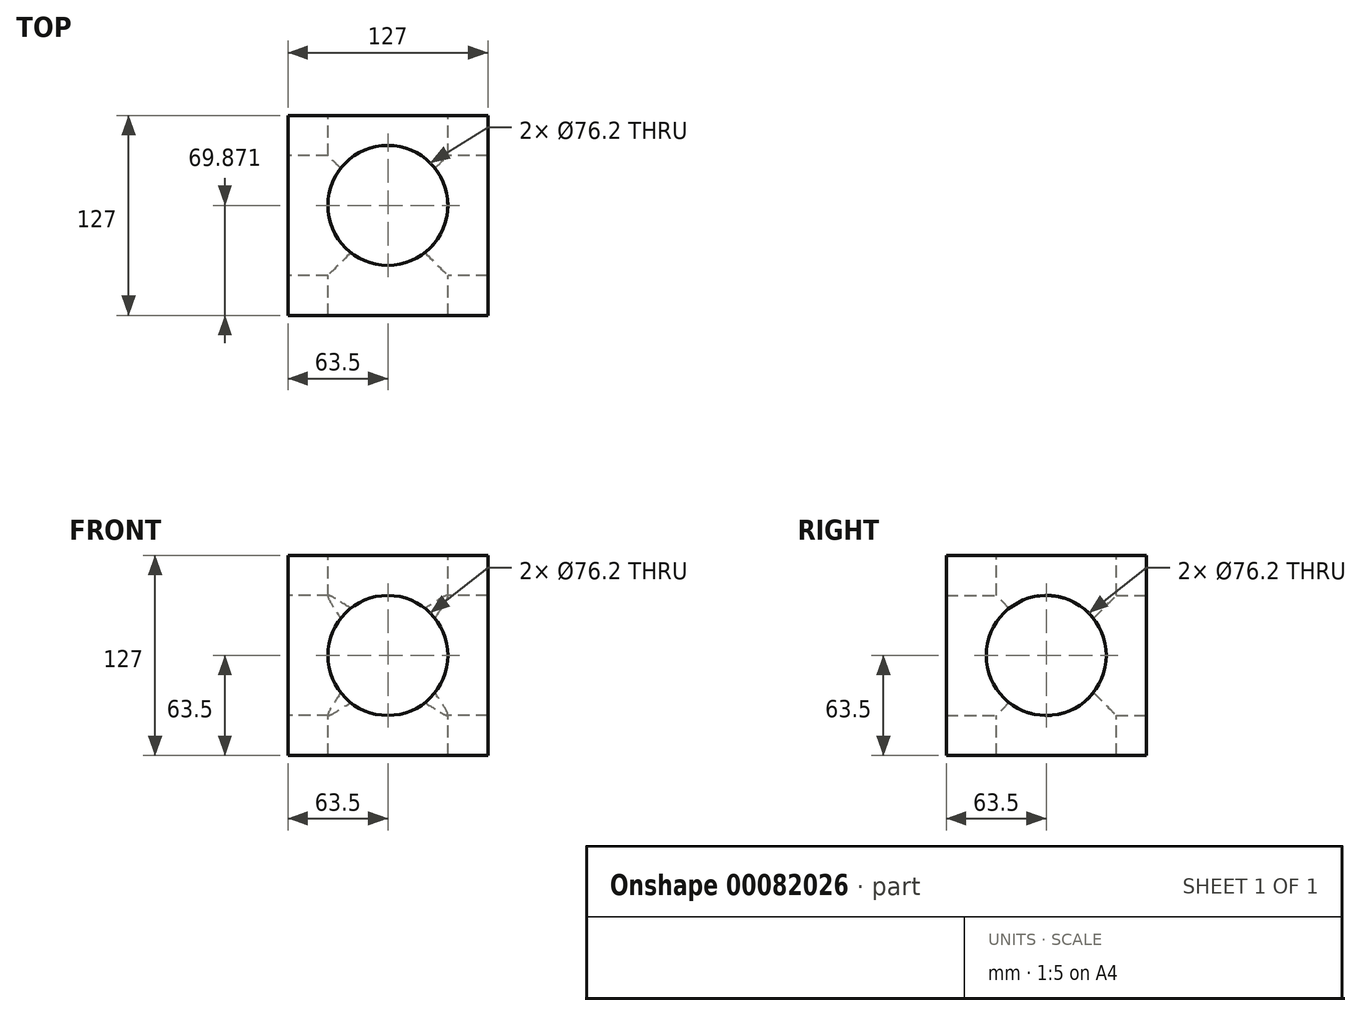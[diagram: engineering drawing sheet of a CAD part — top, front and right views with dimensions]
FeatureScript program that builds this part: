
annotation { "Feature Type Name" : "Feature", "Feature Type Description" : "" }
export const myFeature = defineFeature(function(context is Context, id is Id, definition is map)
    precondition{}
    {
        {
            var Q0;
            Q0=qCreatedBy(makeId("Top.planeOp"),FACE);
            var sketch = newSketch(context, id + "F0", { "sketchPlane" : qUnion([Q0])});
            skLineSegment(sketch, "E0", {"start": v(0, 0) * mm, "end": v(-127, 0) * mm});
            skLineSegment(sketch, "E1", {"start": v(-127, 0) * mm, "end": v(-127, 127) * mm});
            skLineSegment(sketch, "E2", {"start": v(-127, 127) * mm, "end": v(0, 127) * mm});
            skLineSegment(sketch, "E3", {"start": v(0, 0) * mm, "end": v(0, 127) * mm});
            skSolve(sketch);
        }
        {
            var Q0;
            Q0=makeQuery(id+"F0.imprint","IMPRINT",FACE,{"disambiguationData":[TD([[makeQuery(id+"F0.imprint","IMPRINT",EDGE,{"derivedFrom":sQuery(id+"F0.wireOp",EDGE,"E0")}),-1.0]])]});
            extrude(context, id + "F1", {"entities" : qUnion([Q0]), "depth" : 127 * mm});
        }
        {
            var Q0;
            Q0=makeQuery(id+"F1.opExtrude","SWEPT_FACE",FACE,{"disambiguationData":[OSD([sQuery(id+"F0.wireOp",EDGE,"E1")])]});
            var sketch = newSketch(context, id + "F2", { "sketchPlane" : qUnion([Q0])});
            skCircle(sketch, "E4", {"center": v(-63.5, 63.5) * mm, "radius": 38.1 * mm});
            skSolve(sketch);
        }
        {
            var Q0;
            Q0=makeQuery(id+"F1.opExtrude","SWEPT_FACE",FACE,{"disambiguationData":[OSD([sQuery(id+"F0.wireOp",EDGE,"E2")])]});
            var sketch = newSketch(context, id + "F3", { "sketchPlane" : qUnion([Q0])});
            skCircle(sketch, "E5", {"center": v(63.5, 63.5) * mm, "radius": 38.1 * mm});
            skSolve(sketch);
        }
        {
            var Q0;
            Q0=makeQuery(id+"F1.opExtrude","CAP_FACE",FACE,{"disambiguationData":[OSD([sQuery(id+"F0.wireOp",EDGE,"E0"),sQuery(id+"F0.wireOp",EDGE,"E1"),sQuery(id+"F0.wireOp",EDGE,"E2"),sQuery(id+"F0.wireOp",EDGE,"E3")])],"isStart":false});
            var sketch = newSketch(context, id + "F4", { "sketchPlane" : qUnion([Q0])});
            skCircle(sketch, "E6", {"center": v(-63.5, 69.87) * mm, "radius": 38.1 * mm});
            skPoint(sketch, "E7.orphan", {"position": v(-63.5, 127) * mm});
            skPoint(sketch, "E8.end.orphan", {"position": v(-63.5, 0) * mm});
            skSolve(sketch);
        }
        {
            var Q0;
            Q0=makeQuery(id+"F4.imprint","IMPRINT",FACE,{"disambiguationData":[TD([[makeQuery(id+"F4.imprint","IMPRINT",EDGE,{"derivedFrom":sQuery(id+"F4.wireOp",EDGE,"E6")}),1.0]])]});
            extrude(context, id + "F5", {"entities" : qUnion([Q0]), "operationType" : NewBodyOperationType.REMOVE, "oppositeDirection" : true, "depth" : 127 * mm});
        }
        {
            var Q0;
            Q0=makeQuery(id+"F3.imprint","IMPRINT",FACE,{"disambiguationData":[TD([[makeQuery(id+"F3.imprint","IMPRINT",EDGE,{"derivedFrom":sQuery(id+"F3.wireOp",EDGE,"E5")}),1.0]])]});
            extrude(context, id + "F6", {"entities" : qUnion([Q0]), "operationType" : NewBodyOperationType.REMOVE, "oppositeDirection" : true, "depth" : 127 * mm});
        }
        {
            var Q0;
            Q0=makeQuery(id+"F2.imprint","IMPRINT",FACE,{"disambiguationData":[TD([[makeQuery(id+"F2.imprint","IMPRINT",EDGE,{"derivedFrom":sQuery(id+"F2.wireOp",EDGE,"E4")}),1.0]])]});
            extrude(context, id + "F7", {"entities" : qUnion([Q0]), "operationType" : NewBodyOperationType.REMOVE, "oppositeDirection" : true, "depth" : 127 * mm});
        }
    });
